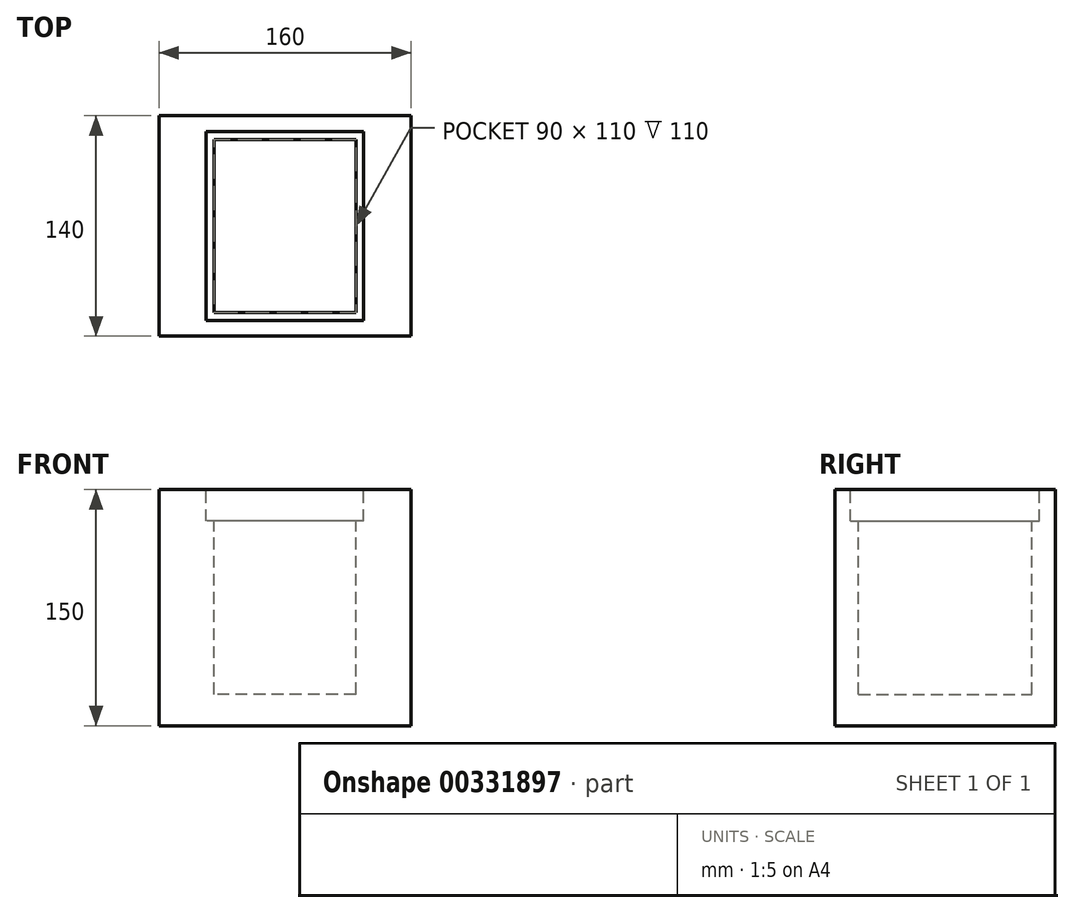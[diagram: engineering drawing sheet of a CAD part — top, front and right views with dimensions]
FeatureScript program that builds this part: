
annotation { "Feature Type Name" : "Feature", "Feature Type Description" : "" }
export const myFeature = defineFeature(function(context is Context, id is Id, definition is map)
    precondition{}
    {
        {
            var Q0;
            Q0=qCreatedBy(makeId("Top.planeOp"),FACE);
            var sketch = newSketch(context, id + "F0", { "sketchPlane" : qUnion([Q0])});
            skLineSegment(sketch, "E0.bottom", {"start": v(80, -70) * mm, "end": v(-80, -70) * mm});
            skLineSegment(sketch, "E0.top", {"start": v(80, 70) * mm, "end": v(-80, 70) * mm});
            skLineSegment(sketch, "E0.left", {"start": v(80, -70) * mm, "end": v(80, 70) * mm});
            skLineSegment(sketch, "E0.right", {"start": v(-80, -70) * mm, "end": v(-80, 70) * mm});
            skPoint(sketch, "E0.middle", {"position": v(0, 0) * mm});
            skSolve(sketch);
        }
        {
            var Q0;
            Q0=makeQuery(id+"F0.imprint","IMPRINT",FACE,{"disambiguationData":[TD([[makeQuery(id+"F0.imprint","IMPRINT",EDGE,{"derivedFrom":sQuery(id+"F0.wireOp",EDGE,"E0.bottom")}),-1.0]])]});
            extrude(context, id + "F1", {"entities" : qUnion([Q0]), "depth" : 150 * mm});
        }
        {
            var Q0;
            Q0=makeQuery(id+"F1.opExtrude","CAP_FACE",FACE,{"disambiguationData":[OSD([sQuery(id+"F0.wireOp",EDGE,"E0.bottom"),sQuery(id+"F0.wireOp",EDGE,"E0.top"),sQuery(id+"F0.wireOp",EDGE,"E0.left"),sQuery(id+"F0.wireOp",EDGE,"E0.right")])],"isStart":false});
            var sketch = newSketch(context, id + "F2", { "sketchPlane" : qUnion([Q0])});
            skLineSegment(sketch, "E1.bottom", {"start": v(50, -60) * mm, "end": v(-50, -60) * mm});
            skLineSegment(sketch, "E1.top", {"start": v(50, 60) * mm, "end": v(-50, 60) * mm});
            skLineSegment(sketch, "E1.left", {"start": v(50, -60) * mm, "end": v(50, 60) * mm});
            skLineSegment(sketch, "E1.right", {"start": v(-50, -60) * mm, "end": v(-50, 60) * mm});
            skPoint(sketch, "E1.middle", {"position": v(0, 0) * mm});
            skSolve(sketch);
        }
        {
            var Q0;
            Q0=makeQuery(id+"F2.imprint","IMPRINT",FACE,{"disambiguationData":[TD([[makeQuery(id+"F2.imprint","IMPRINT",EDGE,{"derivedFrom":sQuery(id+"F2.wireOp",EDGE,"E1.bottom")}),-1.0]])]});
            extrude(context, id + "F3", {"entities" : qUnion([Q0]), "operationType" : NewBodyOperationType.REMOVE, "oppositeDirection" : true, "depth" : 20 * mm});
        }
        {
            var Q0;
            Q0=makeQuery(id+"F3.boolean.opBoolean","COPY",FACE,{"derivedFrom":makeQuery(id+"F3.opExtrude","CAP_FACE",FACE,{"disambiguationData":[OSD([sQuery(id+"F2.wireOp",EDGE,"E1.bottom"),sQuery(id+"F2.wireOp",EDGE,"E1.top"),sQuery(id+"F2.wireOp",EDGE,"E1.left"),sQuery(id+"F2.wireOp",EDGE,"E1.right")])],"isStart":false})});
            var sketch = newSketch(context, id + "F4", { "sketchPlane" : qUnion([Q0])});
            skLineSegment(sketch, "E2.bottom", {"start": v(45, -55) * mm, "end": v(-45, -55) * mm});
            skLineSegment(sketch, "E2.top", {"start": v(45, 55) * mm, "end": v(-45, 55) * mm});
            skLineSegment(sketch, "E2.left", {"start": v(45, -55) * mm, "end": v(45, 55) * mm});
            skLineSegment(sketch, "E2.right", {"start": v(-45, -55) * mm, "end": v(-45, 55) * mm});
            skPoint(sketch, "E2.middle", {"position": v(0, 0) * mm});
            skSolve(sketch);
        }
        {
            var Q0;
            Q0=makeQuery(id+"F4.imprint","IMPRINT",FACE,{"disambiguationData":[TD([[makeQuery(id+"F4.imprint","IMPRINT",EDGE,{"derivedFrom":sQuery(id+"F4.wireOp",EDGE,"E2.bottom")}),-1.0]])]});
            extrude(context, id + "F5", {"entities" : qUnion([Q0]), "operationType" : NewBodyOperationType.REMOVE, "oppositeDirection" : true, "depth" : 110 * mm});
        }
    });
